# Revit family: HeartFelt-Linear-Carrier1-M60_HunterDouglasEurope
name_source: partatom
category: Specialty Equipment
revit_build: Autodesk Revit 2016 (Build: 20150220_1215(x64)
units: mm (PartAtom-declared; Revit-internal decimal feet)

## family parameters
Always vertical = No
Cut with Voids When Loaded = No
OmniClass Number = 23.35.70.24.11.11.11
OmniClass Title = Suspended Ceilings, Suspension Assembly
Part Type = Normal
Room Calculation Point = No
Round Connector Dimension = Use Diameter
Shared = No
Work Plane-Based = No

## types (2) — shared parameters
Alloy = EN AW 5050
Article Code = 332076
Carrier Exact Length = 4975mm
EN13501-1_Fire rating = Class A2,s1,d0
Height = 52 mm
Instalation Instructions = http://assets2.hunterdouglascontract.com
Instructions for Disassembly = http://assets2.hunterdouglascontract.com
Maintenance Instructions = http://assets2.hunterdouglascontract.com
Manufacturer = Hunter Douglas
Model = HeartFelt Carrier 1 M60
Product Data = http://assets2.hunterdouglascontract.com
Product Line = HeartFelt® Linear
Subcategory = HeartFelt® Ceilings
Substrate = Aluminum
System Joint Width = 20mm
System Openness = 33%
System Weight (Panel1 40x55) = 4.3 kg/m²
Thickness = 0.95 mm  [stored 0.0031168 ft]
URL = http://www.hunterdouglasarchitectural.eu

## per-type parameters (varying)
| type | Colour Code | Material |
| HeartFelt AL Carrier1 M60_Transparent Coated | 7178 | Aluminum-7178_HunterDouglasEurope |
| HeartFelt AL Carrier1 M60_Black | 1863 | Aluminum-1863_HunterDouglasEurope |

note: [stored X ft] marks values corroborated as IEEE doubles in the binary element streams (Revit-internal decimal feet)

## geometry (parser evidence)
native form markers: Sweep x5
no freeform markers — native parametric forms only
